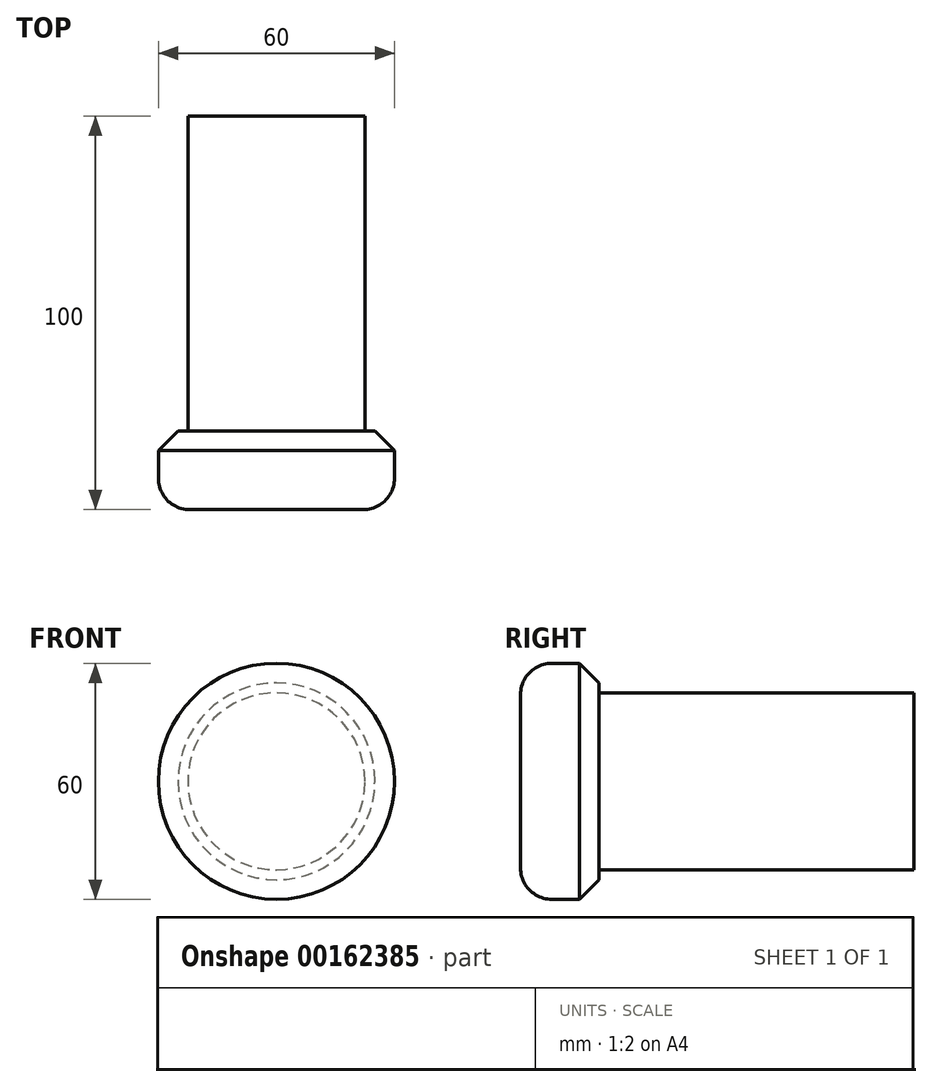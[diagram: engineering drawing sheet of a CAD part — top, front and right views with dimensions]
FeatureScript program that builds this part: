
annotation { "Feature Type Name" : "Feature", "Feature Type Description" : "" }
export const myFeature = defineFeature(function(context is Context, id is Id, definition is map)
    precondition{}
    {
        {
            var Q0;
            Q0=qCreatedBy(makeId("Front.planeOp"),FACE);
            var sketch = newSketch(context, id + "F0", { "sketchPlane" : qUnion([Q0])});
            skCircle(sketch, "E0", {"center": v(0, 0) * mm, "radius": 30 * mm});
            skCircle(sketch, "E1", {"center": v(0, 0) * mm, "radius": 22.5 * mm});
            skSolve(sketch);
        }
        {
            var Q0;
            Q0=makeQuery(id+"F0.imprint","IMPRINT",FACE,{"disambiguationData":[TD([[makeQuery(id+"F0.imprint","IMPRINT",EDGE,{"derivedFrom":sQuery(id+"F0.wireOp",EDGE,"E1")}),1.0]])]});
            var Q1;
            Q1=makeQuery(id+"F0.imprint","IMPRINT",FACE,{"disambiguationData":[TD([[makeQuery(id+"F0.imprint","IMPRINT",EDGE,{"derivedFrom":sQuery(id+"F0.wireOp",EDGE,"E0")}),1.0]])]});
            extrude(context, id + "F1", {"entities" : qUnion([Q0, Q1]), "oppositeDirection" : true, "depth" : 20 * mm});
        }
        {
            var Q0;
            Q0=makeQuery(id+"F0.imprint","IMPRINT",FACE,{"disambiguationData":[TD([[makeQuery(id+"F0.imprint","IMPRINT",EDGE,{"derivedFrom":sQuery(id+"F0.wireOp",EDGE,"E1")}),1.0]])]});
            extrude(context, id + "F2", {"entities" : qUnion([Q0]), "operationType" : NewBodyOperationType.ADD, "oppositeDirection" : true, "depth" : 100 * mm});
        }
        {
            var Q0;
            Q0=makeQuery(id+"F1.opExtrude","CAP_EDGE",EDGE,{"disambiguationData":[OSD([sQuery(id+"F0.wireOp",EDGE,"E0")])],"isStart":false});
            chamfer(context, id + "F3", {"entities" : qUnion([Q0]), "width" : 5 * mm, "tangentPropagation" : true});
        }
        {
            var Q0;
            Q0=makeQuery(id+"F1.opExtrude","CAP_EDGE",EDGE,{"disambiguationData":[OSD([sQuery(id+"F0.wireOp",EDGE,"E0")])],"isStart":true});
            fillet(context, id + "F4", {"entities" : qUnion([Q0]), "radius" : 8 * mm, "tangentPropagation" : true, "allowEdgeOverflow" : false});
        }
    });
